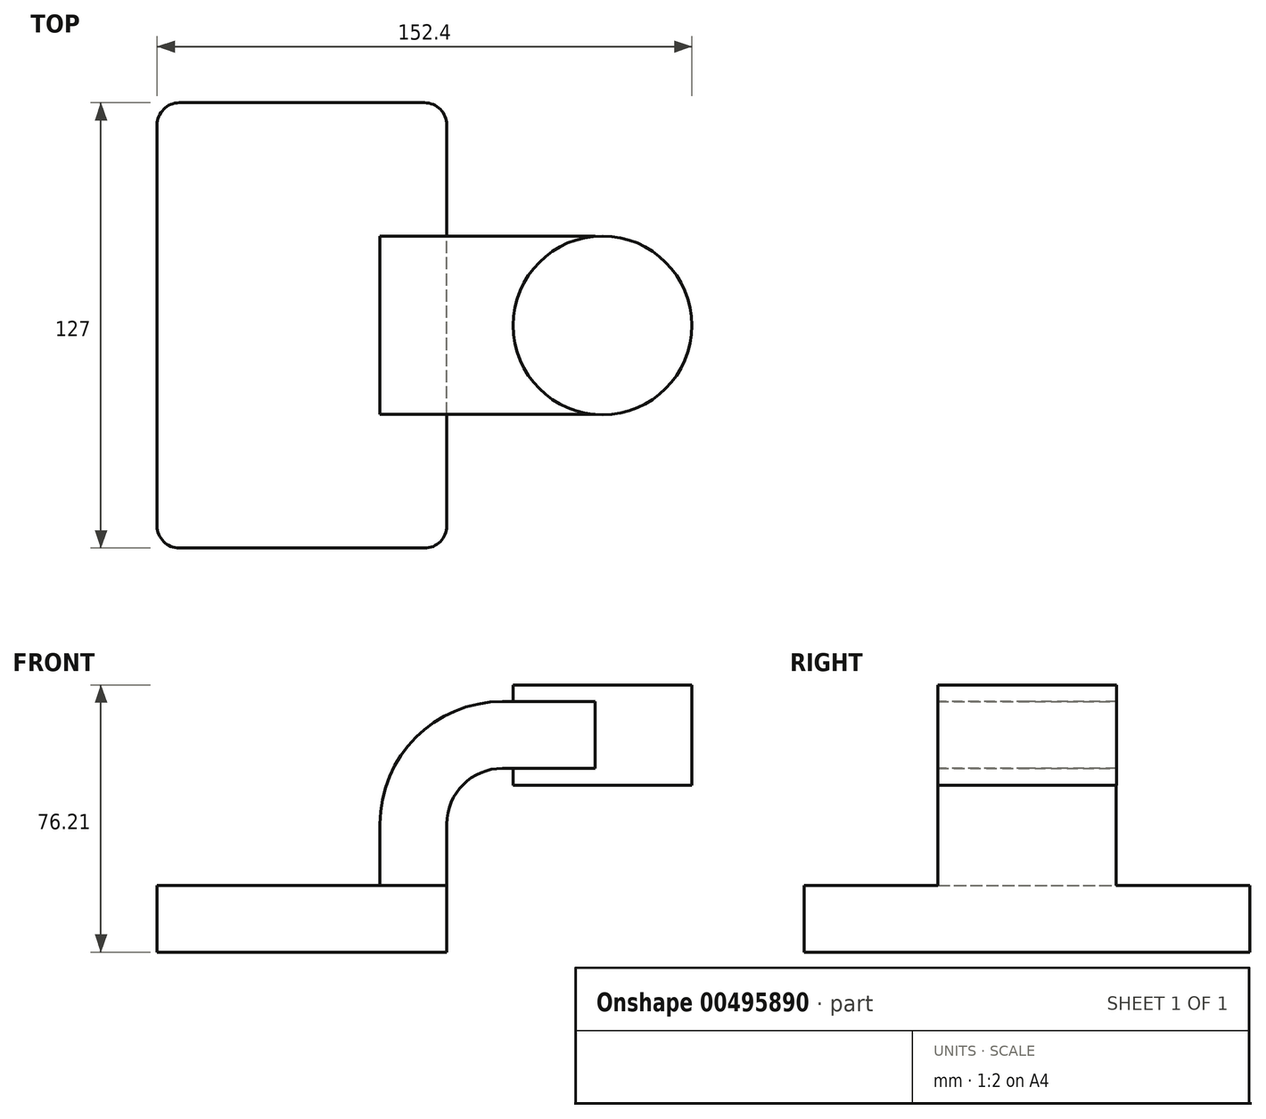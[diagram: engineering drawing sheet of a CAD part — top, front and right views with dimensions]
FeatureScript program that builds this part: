
annotation { "Feature Type Name" : "Feature", "Feature Type Description" : "" }
export const myFeature = defineFeature(function(context is Context, id is Id, definition is map)
    precondition{}
    {
        {
            var Q0;
            Q0=qCreatedBy(makeId("Front.planeOp"),FACE);
            var sketch = newSketch(context, id + "F0", { "sketchPlane" : qUnion([Q0])});
            skLineSegment(sketch, "E0.bottom", {"start": v(41.28, -9.52) * mm, "end": v(-41.28, -9.53) * mm});
            skLineSegment(sketch, "E0.top", {"start": v(41.27, 9.53) * mm, "end": v(-41.28, 9.53) * mm});
            skLineSegment(sketch, "E0.left", {"start": v(41.28, -9.52) * mm, "end": v(41.28, 9.53) * mm});
            skLineSegment(sketch, "E0.right", {"start": v(-41.28, -9.53) * mm, "end": v(-41.28, 9.53) * mm});
            skPoint(sketch, "E0.middle", {"position": v(0, 0) * mm});
            skLineSegment(sketch, "E1.bottom", {"start": v(111.12, 38.1) * mm, "end": v(60.32, 38.1) * mm});
            skLineSegment(sketch, "E1.top", {"start": v(111.12, 66.68) * mm, "end": v(60.32, 66.68) * mm});
            skLineSegment(sketch, "E1.left", {"start": v(111.12, 38.1) * mm, "end": v(111.12, 66.68) * mm});
            skLineSegment(sketch, "E1.right", {"start": v(60.32, 38.1) * mm, "end": v(60.32, 66.67) * mm});
            skPoint(sketch, "E1.middle", {"position": v(85.72, 52.39) * mm});
            skLineSegment(sketch, "E2", {"start": v(41.27, 9.53) * mm, "end": v(41.27, 27) * mm});
            skArc(sketch, "E3", {"start": v(41.27, 27) * mm, "mid": v(45.92, 38.23) * mm, "end": v(57.15, 42.88) * mm});
            skLineSegment(sketch, "E4", {"start": v(57.15, 42.88) * mm, "end": v(85.64, 42.88) * mm});
            skLineSegment(sketch, "E5.0", {"start": v(57.15, 61.93) * mm, "end": v(85.64, 61.93) * mm});
            skArc(sketch, "E5.1", {"start": v(22.23, 27) * mm, "mid": v(32.45, 51.7) * mm, "end": v(57.15, 61.93) * mm});
            skLineSegment(sketch, "E5.2", {"start": v(22.22, 9.53) * mm, "end": v(22.22, 27) * mm});
            skLineSegment(sketch, "E6", {"start": v(85.64, 38.1) * mm, "end": v(85.64, 66.68) * mm});
            skPoint(sketch, "E6.startSnap0", {"position": v(85.72, 38.1) * mm});
            skFitSpline(sketch, "E7", {"points": [v(-41.28, 9.52) * mm, v(57.15, 61.93) * mm], "startDerivative": vector(9.6, 96.44) * mm, "endDerivative": vector(104.6, 0.02) * mm});
            skSolve(sketch);
        }
        {
            var Q0;
            Q0=makeQuery(id+"F0.imprint","IMPRINT",FACE,{"disambiguationData":[TD([[makeQuery(id+"F0.imprint","IMPRINT",EDGE,{"derivedFrom":sQuery(id+"F0.wireOp",EDGE,"E0.bottom")}),-1.0]])]});
            extrude(context, id + "F1", {"entities" : qUnion([Q0]), "endBound" : BoundingType.SYMMETRIC, "depth" : 127 * mm});
        }
        {
            var Q0;
            {var subQ1=sQuery(id+"F0.wireOp",EDGE,"E2");Q0=makeQuery(id+"F0.imprint","IMPRINT",FACE,{"disambiguationData":[TD([[makeQuery(id+"F0.imprint","IMPRINT",EDGE,{"derivedFrom":subQ1}),1.0]])]});}
            var Q1;
            {var subQ0=sQuery(id+"F0.wireOp",EDGE,"E4");var subQ1=sQuery(id+"F0.wireOp",EDGE,"E1.right");var subQ2=makeQuery(id+"F0.imprint","INTERSECT",VERTEX,{"derivedFrom":[subQ1,subQ0]});Q1=makeQuery(id+"F0.imprint","IMPRINT",FACE,{"disambiguationData":[TD([[makeQuery(id+"F0.imprint","IMPRINT",EDGE,{"disambiguationData":[TD([[subQ2,-1.0]])],"derivedFrom":subQ1}),-1.0]])]});}
            extrude(context, id + "F2", {"entities" : qUnion([Q0, Q1]), "operationType" : NewBodyOperationType.ADD, "endBound" : BoundingType.SYMMETRIC, "depth" : 50.8 * mm});
        }
        {
            var Q0;
            Q0=makeQuery(id+"F0.imprint","IMPRINT",FACE,{"disambiguationData":[TD([[makeQuery(id+"F0.imprint","IMPRINT",EDGE,{"derivedFrom":sQuery(id+"F0.wireOp",EDGE,"E5.1")}),1.0]])]});
            extrude(context, id + "F3", {"entities" : qUnion([Q0]), "operationType" : NewBodyOperationType.ADD, "endBound" : BoundingType.SYMMETRIC, "depth" : 15.88 * mm});
        }
        {
            var Q0;
            {var subQ4=sQuery(id+"F0.wireOp",EDGE,"E1.left");Q0=makeQuery(id+"F0.imprint","IMPRINT",FACE,{"disambiguationData":[TD([[makeQuery(id+"F0.imprint","IMPRINT",EDGE,{"derivedFrom":subQ4}),1.0]])]});}
            var Q1;
            Q1=sQuery(id+"F0.wireOp",EDGE,"E6");
            revolve(context, id + "F4", {"operationType" : NewBodyOperationType.ADD, "entities" : qUnion([Q0]), "axis" : qUnion([Q1]), "revolveType" : RevolveType.FULL});
        }
        {
            var Q0;
            Q0=makeQuery(id+"F1.opExtrude","CAP_EDGE",EDGE,{"disambiguationData":[OSD([sQuery(id+"F0.wireOp",EDGE,"E0.left")])],"isStart":false});
            var Q1;
            Q1=makeQuery(id+"F1.opExtrude","CAP_EDGE",EDGE,{"disambiguationData":[OSD([sQuery(id+"F0.wireOp",EDGE,"E0.right")])],"isStart":false});
            var Q2;
            Q2=makeQuery(id+"F1.opExtrude","CAP_EDGE",EDGE,{"disambiguationData":[OSD([sQuery(id+"F0.wireOp",EDGE,"E0.left")])],"isStart":true});
            var Q3;
            Q3=makeQuery(id+"F1.opExtrude","CAP_EDGE",EDGE,{"disambiguationData":[OSD([sQuery(id+"F0.wireOp",EDGE,"E0.right")])],"isStart":true});
            fillet(context, id + "F5", {"entities" : qUnion([Q0, Q1, Q2, Q3]), "radius" : 6.35 * mm, "tangentPropagation" : true, "allowEdgeOverflow" : false});
        }
    });
